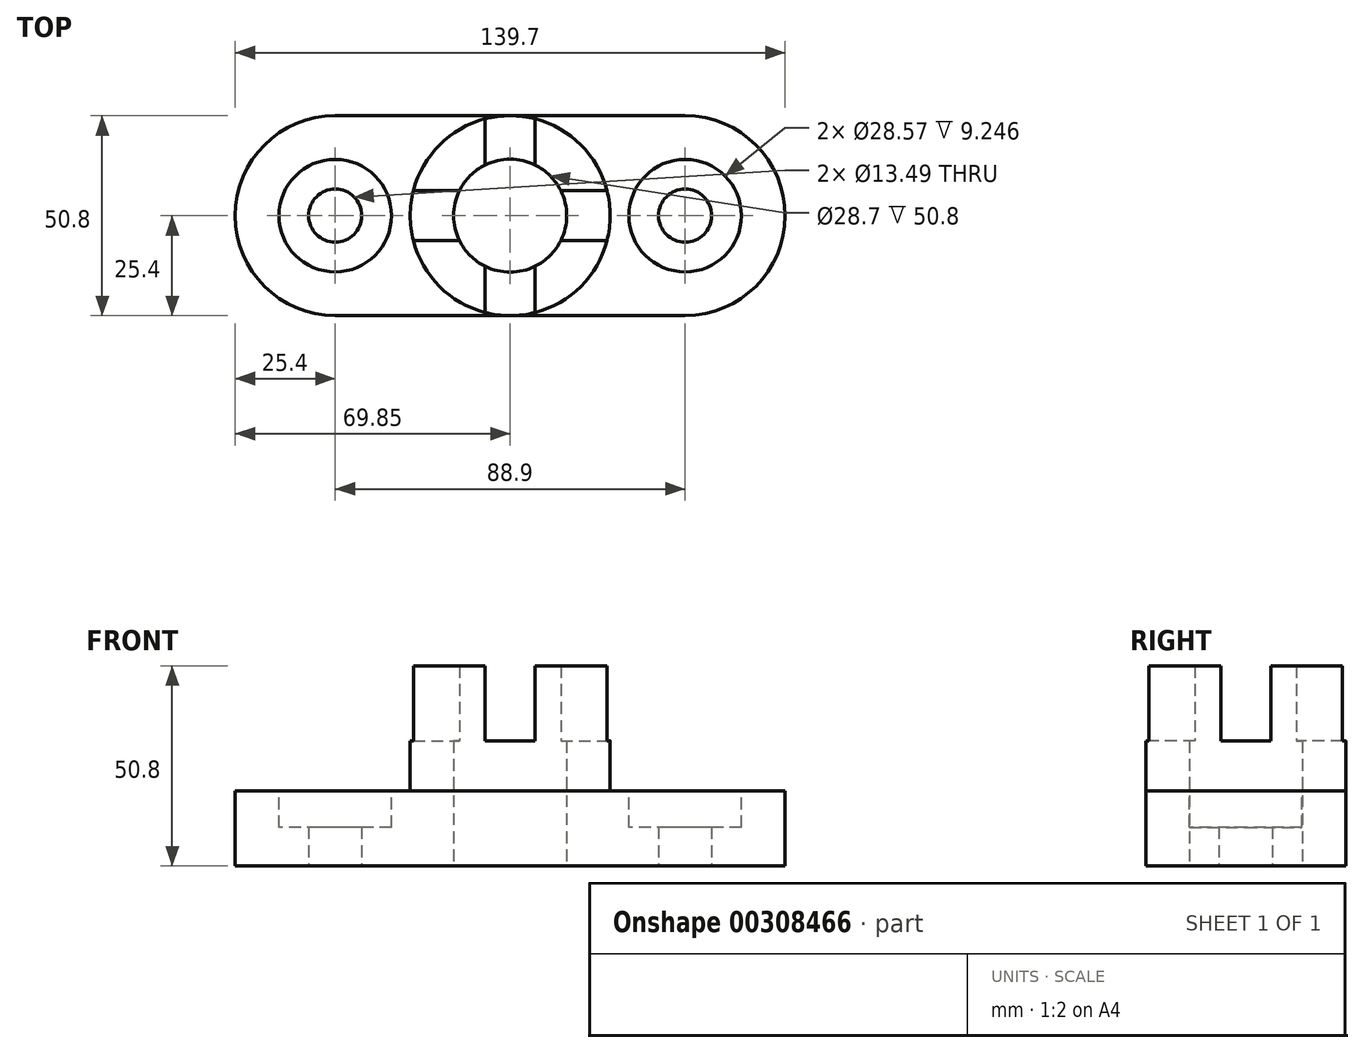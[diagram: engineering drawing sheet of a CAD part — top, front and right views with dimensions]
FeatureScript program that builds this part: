
annotation { "Feature Type Name" : "Feature", "Feature Type Description" : "" }
export const myFeature = defineFeature(function(context is Context, id is Id, definition is map)
    precondition{}
    {
        {
            var Q0;
            Q0=qCreatedBy(makeId("Top.planeOp"),FACE);
            var sketch = newSketch(context, id + "F0", { "sketchPlane" : qUnion([Q0])});
            skLineSegment(sketch, "E0", {"start": v(-44.45, 0) * mm, "end": v(44.45, 0) * mm, "construction": true});
            skArc(sketch, "E1.0.startCap", {"start": v(-44.45, -25.4) * mm, "mid": v(-69.85, 0) * mm, "end": v(-44.45, 25.4) * mm});
            skArc(sketch, "E1.0.endCap", {"start": v(44.45, 25.4) * mm, "mid": v(69.85, 0) * mm, "end": v(44.45, -25.4) * mm});
            skLineSegment(sketch, "E1.0.left", {"start": v(-44.45, 25.4) * mm, "end": v(44.45, 25.4) * mm});
            skLineSegment(sketch, "E1.0.right", {"start": v(-44.45, -25.4) * mm, "end": v(44.45, -25.4) * mm});
            skSolve(sketch);
        }
        {
            var Q0;
            Q0 = qSketchRegion(id + "F0", true);
            extrude(context, id + "F1", {"entities" : qUnion([Q0]), "depth" : 19.05 * mm});
        }
        {
            var Q0;
            Q0=makeQuery(id+"F1.opExtrude","CAP_FACE",FACE,{"disambiguationData":[OSD([sQuery(id+"F0.wireOp",EDGE,"E1.0.startCap"),sQuery(id+"F0.wireOp",EDGE,"E1.0.endCap"),sQuery(id+"F0.wireOp",EDGE,"E1.0.left"),sQuery(id+"F0.wireOp",EDGE,"E1.0.right")])],"isStart":false});
            var sketch = newSketch(context, id + "F2", { "sketchPlane" : qUnion([Q0])});
            skCircle(sketch, "E2", {"center": v(-44.45, 0) * mm, "radius": 14.29 * mm});
            skCircle(sketch, "E3", {"center": v(44.45, 0) * mm, "radius": 14.29 * mm});
            skSolve(sketch);
        }
        {
            var Q0;
            Q0 = qSketchRegion(id + "F2", true);
            extrude(context, id + "F3", {"entities" : qUnion([Q0]), "operationType" : NewBodyOperationType.REMOVE, "oppositeDirection" : true, "depth" : 9.25 * mm});
        }
        {
            var Q0;
            Q0=makeQuery(id+"F1.opExtrude","CAP_FACE",FACE,{"disambiguationData":[OSD([sQuery(id+"F0.wireOp",EDGE,"E1.0.startCap"),sQuery(id+"F0.wireOp",EDGE,"E1.0.endCap"),sQuery(id+"F0.wireOp",EDGE,"E1.0.left"),sQuery(id+"F0.wireOp",EDGE,"E1.0.right")])],"isStart":true});
            var sketch = newSketch(context, id + "F4", { "sketchPlane" : qUnion([Q0])});
            skCircle(sketch, "E4", {"center": v(-44.45, 0) * mm, "radius": 6.74 * mm});
            skCircle(sketch, "E5", {"center": v(44.45, 0) * mm, "radius": 6.74 * mm});
            skSolve(sketch);
        }
        {
            var Q0;
            Q0 = qSketchRegion(id + "F4", true);
            extrude(context, id + "F5", {"entities" : qUnion([Q0]), "operationType" : NewBodyOperationType.REMOVE, "endBound" : BoundingType.THROUGH_ALL, "oppositeDirection" : true, "depth" : 25.4 * mm});
        }
        {
            var Q0;
            Q0=makeQuery(id+"F1.opExtrude","CAP_FACE",FACE,{"disambiguationData":[OSD([sQuery(id+"F0.wireOp",EDGE,"E1.0.startCap"),sQuery(id+"F0.wireOp",EDGE,"E1.0.endCap"),sQuery(id+"F0.wireOp",EDGE,"E1.0.left"),sQuery(id+"F0.wireOp",EDGE,"E1.0.right")])],"isStart":false});
            var sketch = newSketch(context, id + "F6", { "sketchPlane" : qUnion([Q0])});
            skCircle(sketch, "E6", {"center": v(0, 0) * mm, "radius": 25.4 * mm});
            skCircle(sketch, "E7", {"center": v(0, 0) * mm, "radius": 14.35 * mm});
            skSolve(sketch);
        }
        {
            var Q0;
            Q0 = qSketchRegion(id + "F6", true);
            extrude(context, id + "F7", {"entities" : qUnion([Q0]), "operationType" : NewBodyOperationType.ADD, "depth" : 31.75 * mm});
        }
        {
            var Q0;
            Q0=qCreatedBy(makeId("Front.planeOp"),FACE);
            var sketch = newSketch(context, id + "F8", { "sketchPlane" : qUnion([Q0])});
            skLineSegment(sketch, "E8", {"start": v(0, 0) * mm, "end": v(0, 31.75) * mm, "construction": true});
            skLineSegment(sketch, "E9.bottom", {"start": v(-6.35, 31.75) * mm, "end": v(6.35, 31.75) * mm});
            skLineSegment(sketch, "E9.top", {"start": v(-6.35, 50.8) * mm, "end": v(6.35, 50.8) * mm});
            skLineSegment(sketch, "E9.left", {"start": v(-6.35, 31.75) * mm, "end": v(-6.35, 50.8) * mm});
            skLineSegment(sketch, "E9.right", {"start": v(6.35, 31.75) * mm, "end": v(6.35, 50.8) * mm});
            skSolve(sketch);
        }
        {
            var Q0;
            Q0=makeQuery(id+"F8.imprint","IMPRINT",FACE,{"disambiguationData":[TD([[makeQuery(id+"F8.imprint","IMPRINT",EDGE,{"derivedFrom":sQuery(id+"F8.wireOp",EDGE,"E9.bottom")}),1.0]])]});
            extrude(context, id + "F9", {"entities" : qUnion([Q0]), "operationType" : NewBodyOperationType.REMOVE, "endBound" : BoundingType.THROUGH_ALL, "oppositeDirection" : true, "depth" : 25.4 * mm, "hasSecondDirection" : true, "secondDirectionBound" : SecondDirectionBoundingType.THROUGH_ALL, "secondDirectionOppositeDirection" : false, "secondDirectionDepth" : 25.4 * mm});
        }
        {
            var Q0;
            Q0=qCreatedBy(makeId("Right.planeOp"),FACE);
            var sketch = newSketch(context, id + "F10", { "sketchPlane" : qUnion([Q0])});
            skLineSegment(sketch, "E10", {"start": v(0, 0) * mm, "end": v(0, 31.75) * mm, "construction": true});
            skLineSegment(sketch, "E11.bottom", {"start": v(-6.35, 31.75) * mm, "end": v(6.35, 31.75) * mm});
            skLineSegment(sketch, "E11.top", {"start": v(-6.35, 50.8) * mm, "end": v(6.35, 50.8) * mm});
            skLineSegment(sketch, "E11.left", {"start": v(-6.35, 31.75) * mm, "end": v(-6.35, 50.8) * mm});
            skLineSegment(sketch, "E11.right", {"start": v(6.35, 31.75) * mm, "end": v(6.35, 50.8) * mm});
            skSolve(sketch);
        }
        {
            var Q0;
            Q0 = qSketchRegion(id + "F10", true);
            extrude(context, id + "F11", {"entities" : qUnion([Q0]), "operationType" : NewBodyOperationType.REMOVE, "endBound" : BoundingType.THROUGH_ALL, "oppositeDirection" : true, "depth" : 25.4 * mm, "hasSecondDirection" : true, "secondDirectionBound" : SecondDirectionBoundingType.THROUGH_ALL, "secondDirectionOppositeDirection" : false, "secondDirectionDepth" : 25.4 * mm});
        }
        {
            var Q0;
            Q0=makeQuery(id+"F7.boolean.opBoolean","SPLIT",FACE,{"disambiguationData":[TD([makeQuery(id+"F7.opExtrude","SWEPT_FACE",FACE,{"disambiguationData":[OSD([sQuery(id+"F6.wireOp",EDGE,"E7")])]})])],"derivedFrom":makeQuery(id+"F1.opExtrude","CAP_FACE",FACE,{"disambiguationData":[OSD([sQuery(id+"F0.wireOp",EDGE,"E1.0.startCap"),sQuery(id+"F0.wireOp",EDGE,"E1.0.endCap"),sQuery(id+"F0.wireOp",EDGE,"E1.0.left"),sQuery(id+"F0.wireOp",EDGE,"E1.0.right")])],"isStart":false})});
            extrude(context, id + "F12", {"entities" : qUnion([Q0]), "operationType" : NewBodyOperationType.REMOVE, "endBound" : BoundingType.THROUGH_ALL, "oppositeDirection" : true, "depth" : 25.4 * mm});
        }
    });
